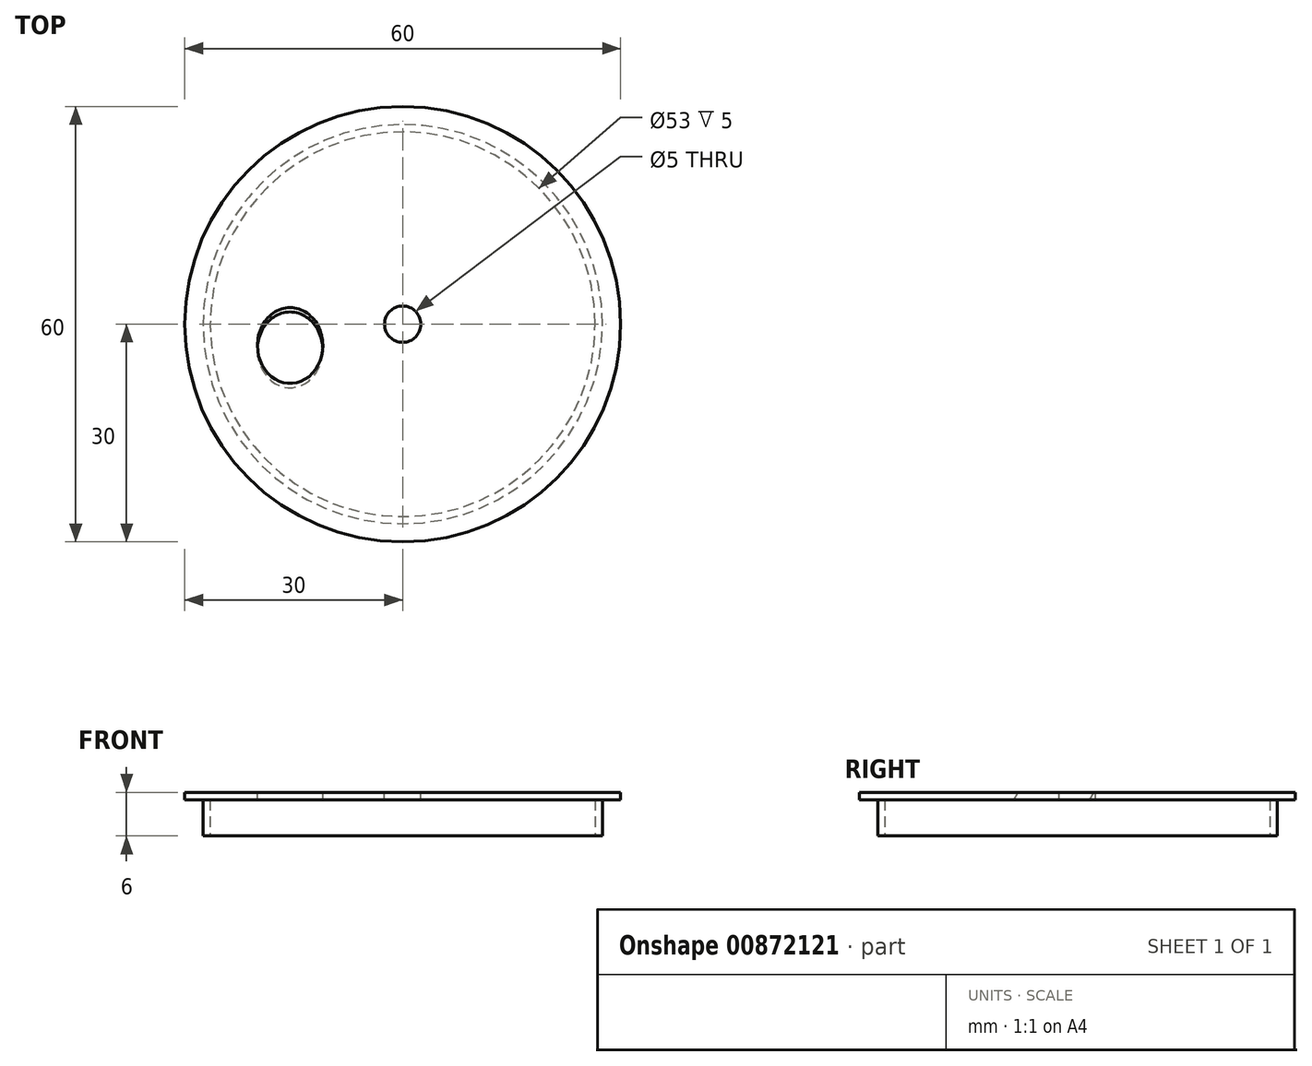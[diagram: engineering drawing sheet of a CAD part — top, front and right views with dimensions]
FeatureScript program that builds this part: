
annotation { "Feature Type Name" : "Feature", "Feature Type Description" : "" }
export const myFeature = defineFeature(function(context is Context, id is Id, definition is map)
    precondition{}
    {
        {
            var Q0;
            Q0=qCreatedBy(makeId("Top.planeOp"),FACE);
            var sketch = newSketch(context, id + "F0", { "sketchPlane" : qUnion([Q0])});
            skCircle(sketch, "E0", {"center": v(0, 0) * mm, "radius": 27.5 * mm});
            skCircle(sketch, "E1", {"center": v(0, 0) * mm, "radius": 26.5 * mm});
            skSolve(sketch);
        }
        {
            var Q0;
            Q0 = qSketchRegion(id + "F0", true);
            extrude(context, id + "F1", {"entities" : qUnion([Q0]), "depth" : 5 * mm, "offsetDistance" : 25 * mm});
        }
        {
            var Q0;
            Q0=makeQuery(id+"F1.opExtrude","CAP_FACE",FACE,{"disambiguationData":[OSD([sQuery(id+"F0.wireOp",EDGE,"E0"),sQuery(id+"F0.wireOp",EDGE,"E1")])],"isStart":false});
            var sketch = newSketch(context, id + "F2", { "sketchPlane" : qUnion([Q0])});
            skCircle(sketch, "E2", {"center": v(0, 0) * mm, "radius": 27.5 * mm});
            skSolve(sketch);
        }
        {
            var Q0;
            Q0 = qSketchRegion(id + "F2", true);
            extrude(context, id + "F3", {"entities" : qUnion([Q0]), "operationType" : NewBodyOperationType.ADD, "depth" : 1 * mm, "offsetDistance" : 25 * mm});
        }
        {
            var Q0;
            Q0=qCreatedBy(makeId("Right.planeOp"),FACE);
            var sketch = newSketch(context, id + "F4", { "sketchPlane" : qUnion([Q0])});
            skLineSegment(sketch, "E3", {"start": v(0, 0) * mm, "end": v(0, 6) * mm, "construction": true});
            skLineSegment(sketch, "E4", {"start": v(0, 6) * mm, "end": v(8.5, 6) * mm});
            skLineSegment(sketch, "E5", {"start": v(0, 6) * mm, "end": v(-8.5, 6) * mm});
            skLineSegment(sketch, "E6", {"start": v(-8.5, 6) * mm, "end": v(-8.5, 16) * mm});
            skLineSegment(sketch, "E7", {"start": v(-8.5, 16) * mm, "end": v(8.5, 6) * mm});
            skSolve(sketch);
        }
        {
            var Q0;
            Q0 = qSketchRegion(id + "F4", true);
            extrude(context, id + "F5", {"entities" : qUnion([Q0]), "operationType" : NewBodyOperationType.ADD, "oppositeDirection" : true, "depth" : 25 * mm, "offsetDistance" : 25 * mm});
        }
        {
            var Q0;
            Q0=makeQuery(id+"F5.opExtrude","CAP_FACE",FACE,{"disambiguationData":[OSD([sQuery(id+"F4.wireOp",EDGE,"E4"),sQuery(id+"F4.wireOp",EDGE,"E5"),sQuery(id+"F4.wireOp",EDGE,"E6"),sQuery(id+"F4.wireOp",EDGE,"E7")])],"isStart":true});
            extrude(context, id + "F6", {"entities" : qUnion([Q0]), "operationType" : NewBodyOperationType.REMOVE, "oppositeDirection" : true, "depth" : 6 * mm, "offsetDistance" : 25 * mm});
        }
        {
            var Q0;
            Q0=makeQuery(id+"F5.opExtrude","SWEPT_FACE",FACE,{"disambiguationData":[OSD([sQuery(id+"F4.wireOp",EDGE,"E7")])]});
            var sketch = newSketch(context, id + "F7", { "sketchPlane" : qUnion([Q0])});
            skLineSegment(sketch, "E8", {"start": v(-25, -5.58) * mm, "end": v(-6, -5.58) * mm, "construction": true});
            skPoint(sketch, "E9", {"position": v(-15.5, -5.58) * mm});
            skSolve(sketch);
        }
        {
            var Q0;
            Q0=sQuery(id+"F7.wireOp",VERTEX,"E9");
            var Q1;
            Q1=makeQuery(id+"F1.opExtrude","SWEPT_BODY",BODY,{"disambiguationData":[OSD([sQuery(id+"F0.wireOp",EDGE,"E0"),sQuery(id+"F0.wireOp",EDGE,"E1")])]});
            hole(context, id + "F8", {"style" : HoleStyle.SIMPLE, "endStyle" : HoleEndStyle.BLIND, "holeDiameter" : 9 * mm, "majorDiameter" : 5 * mm, "holeDepth" : 30 * mm, "isTappedThrough" : true, "tappedDepth" : 12 * mm, "tapClearance" : 3, "locations" : qUnion([Q0]), "scope" : qUnion([Q1])});
        }
        {
            var Q0;
            Q0=makeQuery(id+"F5.opExtrude","CAP_FACE",FACE,{"disambiguationData":[OSD([sQuery(id+"F4.wireOp",EDGE,"E4"),sQuery(id+"F4.wireOp",EDGE,"E5"),sQuery(id+"F4.wireOp",EDGE,"E6"),sQuery(id+"F4.wireOp",EDGE,"E7")])],"isStart":false});
            extrude(context, id + "F9", {"entities" : qUnion([Q0]), "operationType" : NewBodyOperationType.REMOVE, "oppositeDirection" : true, "depth" : 25 * mm, "offsetDistance" : 25 * mm});
        }
        {
            var Q0;
            {var subQ0=sQuery(id+"F4.wireOp",EDGE,"E5");var subQ1=sQuery(id+"F4.wireOp",EDGE,"E4");Q0=makeQuery(id+"F9.boolean.opBoolean","MERGE",FACE,{"derivedFrom":[makeQuery(id+"F6.boolean.opBoolean","MERGE",FACE,{"derivedFrom":[makeQuery(id+"F3.opExtrude","CAP_FACE",FACE,{"disambiguationData":[OSD([sQuery(id+"F2.wireOp",EDGE,"E2")])],"isStart":false})],"fromTools":[makeQuery(id+"F6.opExtrude","SWEPT_FACE",FACE,{"disambiguationData":[OSD([subQ1,subQ0])]})]})],"fromTools":[makeQuery(id+"F9.opExtrude","SWEPT_FACE",FACE,{"disambiguationData":[OSD([subQ1,subQ0])]})]});}
            var sketch = newSketch(context, id + "F10", { "sketchPlane" : qUnion([Q0])});
            skPoint(sketch, "E10", {"position": v(0, 0) * mm});
            skSolve(sketch);
        }
        {
            var Q0;
            Q0=sQuery(id+"F10.wireOp",VERTEX,"E10");
            var Q1;
            Q1=makeQuery(id+"F1.opExtrude","SWEPT_BODY",BODY,{"disambiguationData":[OSD([sQuery(id+"F0.wireOp",EDGE,"E0"),sQuery(id+"F0.wireOp",EDGE,"E1")])]});
            hole(context, id + "F11", {"style" : HoleStyle.SIMPLE, "endStyle" : HoleEndStyle.BLIND, "holeDiameter" : 5 * mm, "majorDiameter" : 5 * mm, "holeDepth" : 30 * mm, "isTappedThrough" : true, "tappedDepth" : 12 * mm, "tapClearance" : 3, "locations" : qUnion([Q0]), "scope" : qUnion([Q1])});
        }
        {
            var Q0;
            {var subQ0=sQuery(id+"F4.wireOp",EDGE,"E5");var subQ1=sQuery(id+"F4.wireOp",EDGE,"E4");Q0=makeQuery(id+"F9.boolean.opBoolean","MERGE",FACE,{"derivedFrom":[makeQuery(id+"F6.boolean.opBoolean","MERGE",FACE,{"derivedFrom":[makeQuery(id+"F3.opExtrude","CAP_FACE",FACE,{"disambiguationData":[OSD([sQuery(id+"F2.wireOp",EDGE,"E2")])],"isStart":false})],"fromTools":[makeQuery(id+"F6.opExtrude","SWEPT_FACE",FACE,{"disambiguationData":[OSD([subQ1,subQ0])]})]})],"fromTools":[makeQuery(id+"F9.opExtrude","SWEPT_FACE",FACE,{"disambiguationData":[OSD([subQ1,subQ0])]})]});}
            var sketch = newSketch(context, id + "F12", { "sketchPlane" : qUnion([Q0])});
            skCircle(sketch, "E11", {"center": v(0, 0) * mm, "radius": 30 * mm});
            skSolve(sketch);
        }
        {
            var Q0;
            Q0=makeQuery(id+"F12.imprint","IMPRINT",FACE,{"disambiguationData":[TD([[makeQuery(id+"F12.imprint","IMPRINT",EDGE,{"derivedFrom":sQuery(id+"F12.wireOp",EDGE,"E11")}),1.0]])]});
            extrude(context, id + "F13", {"entities" : qUnion([Q0]), "operationType" : NewBodyOperationType.ADD, "oppositeDirection" : true, "depth" : 1 * mm, "offsetDistance" : 25 * mm});
        }
    });
